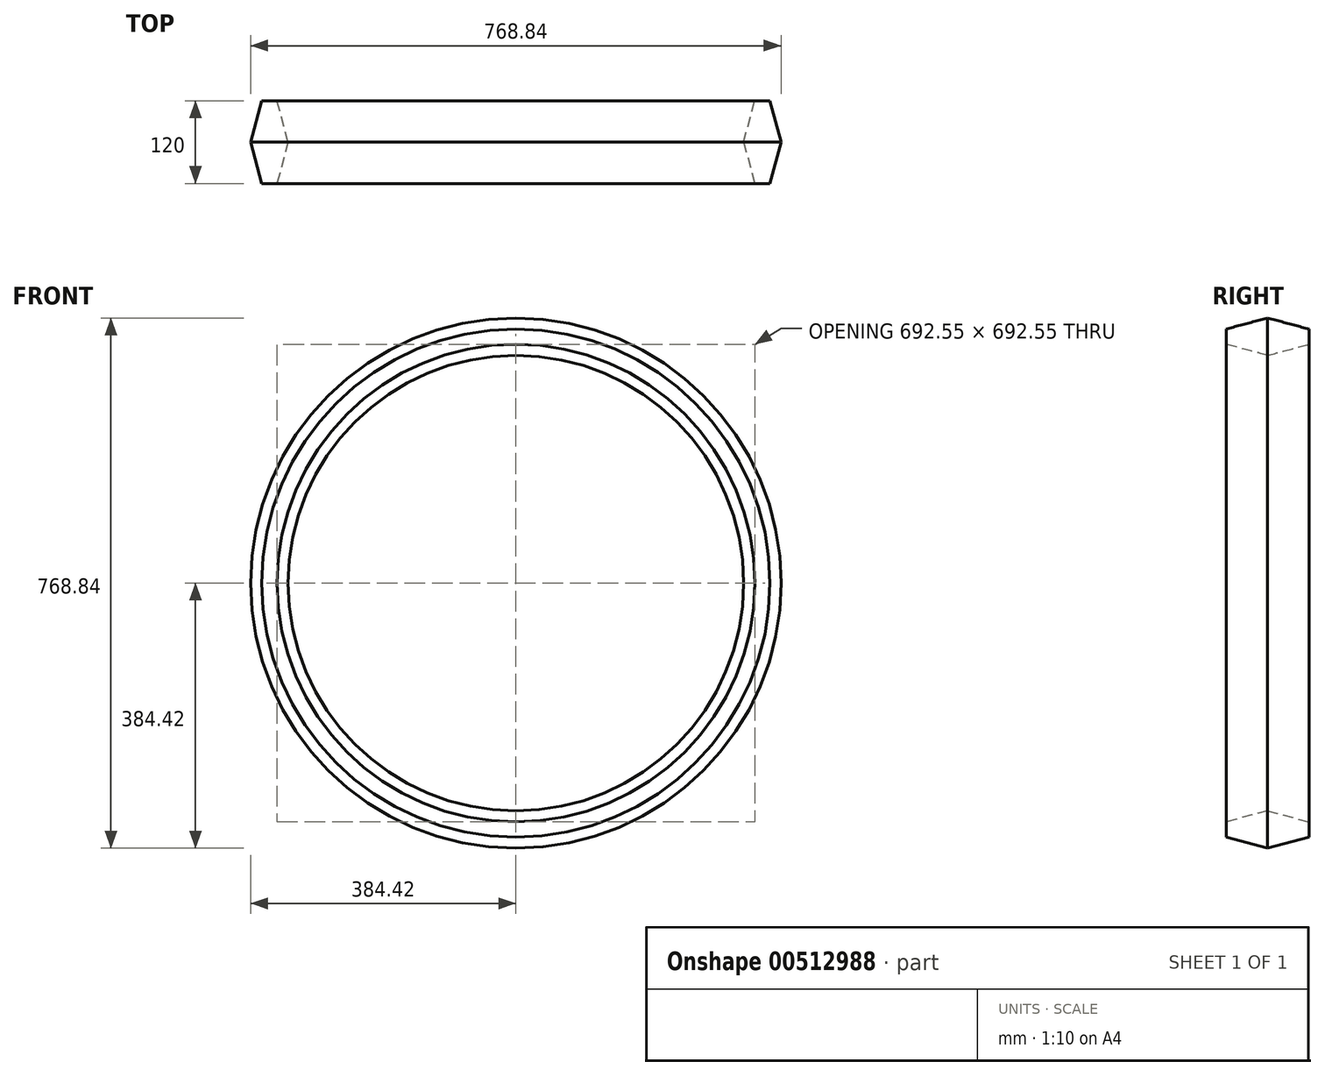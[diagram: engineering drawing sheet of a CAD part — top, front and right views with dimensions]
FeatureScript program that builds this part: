
annotation { "Feature Type Name" : "Feature", "Feature Type Description" : "" }
export const myFeature = defineFeature(function(context is Context, id is Id, definition is map)
    precondition{}
    {
        {
            var Q0;
            Q0=qCreatedBy(makeId("Front.planeOp"),FACE);
            var sketch = newSketch(context, id + "F0", { "sketchPlane" : qUnion([Q0])});
            skLineSegment(sketch, "E0", {"start": v(0, 0) * mm, "end": v(-330.2, 0) * mm});
            skCircle(sketch, "E1", {"center": v(0, 0) * mm, "radius": 330.2 * mm});
            skLineSegment(sketch, "E2", {"start": v(0, 0) * mm, "end": v(-260.21, -203.28) * mm});
            skLineSegment(sketch, "E3", {"start": v(0, 0) * mm, "end": v(0, -330.2) * mm});
            skLineSegment(sketch, "E4", {"start": v(0, 0) * mm, "end": v(0, 330.2) * mm});
            skLineSegment(sketch, "E5", {"start": v(0, 0) * mm, "end": v(330.2, 0) * mm});
            skLineSegment(sketch, "E6", {"start": v(0, 0) * mm, "end": v(245.6, -220.71) * mm});
            skLineSegment(sketch, "E7", {"start": v(0, 0) * mm, "end": v(260.21, 203.28) * mm});
            skLineSegment(sketch, "E8", {"start": v(0, 0) * mm, "end": v(-245.6, 220.71) * mm});
            skLineSegment(sketch, "E9", {"start": v(0, 0) * mm, "end": v(-151.84, -293.22) * mm});
            skLineSegment(sketch, "E10", {"start": v(0, 0) * mm, "end": v(138.6, 299.7) * mm});
            skLineSegment(sketch, "E11", {"start": v(0, 0) * mm, "end": v(311.3, -110.12) * mm});
            skLineSegment(sketch, "E12", {"start": v(0, 0) * mm, "end": v(-312.27, 107.33) * mm});
            skLineSegment(sketch, "E13", {"start": v(0, 0) * mm, "end": v(-122.8, 306.52) * mm});
            skPoint(sketch, "E13.endSnap0", {"position": v(-122.8, 110.36) * mm});
            skLineSegment(sketch, "E14", {"start": v(0, 0) * mm, "end": v(306.52, 122.8) * mm});
            skLineSegment(sketch, "E15", {"start": v(0, 0) * mm, "end": v(122.8, -306.52) * mm});
            skLineSegment(sketch, "E16", {"start": v(0, 0) * mm, "end": v(-306.52, -122.8) * mm});
            skCircle(sketch, "E17", {"center": v(0, 0) * mm, "radius": 384.42 * mm});
            skSolve(sketch);
        }
        {
            var Q0;
            Q0 = qSketchRegion(id + "F0", true);
            extrude(context, id + "F1", {"entities" : qUnion([Q0]), "endBound" : BoundingType.SYMMETRIC, "oppositeDirection" : true, "depth" : 120 * mm, "hasDraft" : true, "draftAngle" : 15 * degree, "draftPullDirection" : true, "hasSecondDirection" : true, "secondDirectionOppositeDirection" : false, "secondDirectionDepth" : 25 * mm});
        }
    });
